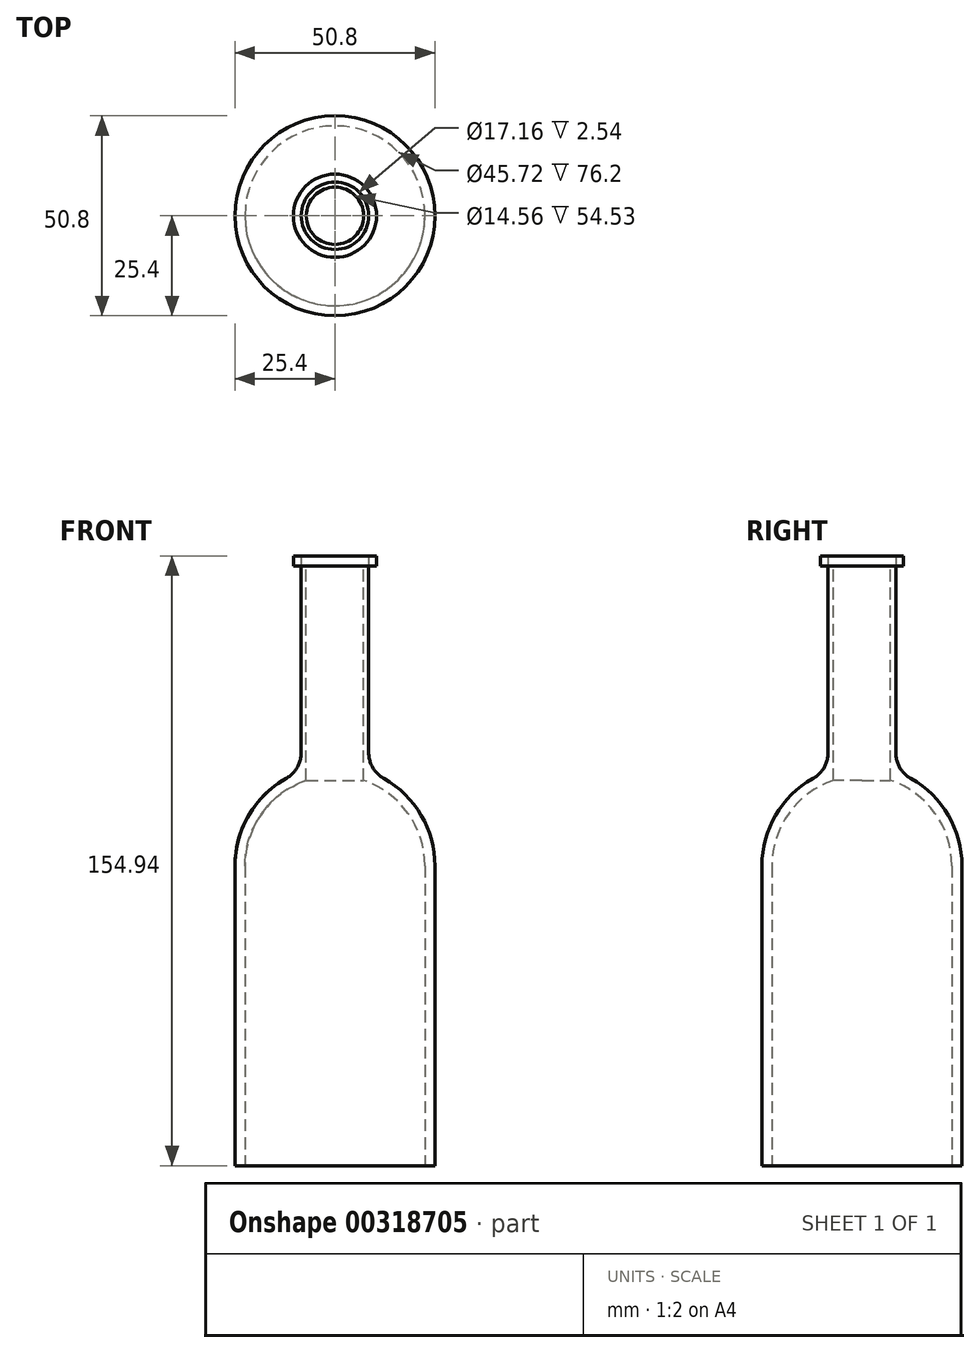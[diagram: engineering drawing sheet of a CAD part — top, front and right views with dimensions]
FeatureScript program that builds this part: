
annotation { "Feature Type Name" : "Feature", "Feature Type Description" : "" }
export const myFeature = defineFeature(function(context is Context, id is Id, definition is map)
    precondition{}
    {
        {
            var Q0;
            Q0=qCreatedBy(makeId("Top.planeOp"),FACE);
            var sketch = newSketch(context, id + "F0", { "sketchPlane" : qUnion([Q0])});
            skCircle(sketch, "E0", {"center": v(0, 0) * mm, "radius": 25.4 * mm});
            skSolve(sketch);
        }
        {
            var Q0;
            Q0=makeQuery(id+"F0.imprint","IMPRINT",FACE,{"disambiguationData":[TD([[makeQuery(id+"F0.imprint","IMPRINT",EDGE,{"derivedFrom":sQuery(id+"F0.wireOp",EDGE,"E0")}),1.0]])]});
            extrude(context, id + "F1", {"entities" : qUnion([Q0]), "depth" : 101.6 * mm});
        }
        {
            var Q0;
            Q0=makeQuery(id+"F1.opExtrude","CAP_EDGE",EDGE,{"disambiguationData":[OSD([sQuery(id+"F0.wireOp",EDGE,"E0")])],"isStart":false});
            fillet(context, id + "F2", {"entities" : qUnion([Q0]), "radius" : 25.4 * mm, "tangentPropagation" : true, "allowEdgeOverflow" : false});
        }
        {
            var Q0;
            Q0=qCreatedBy(makeId("Top.planeOp"),FACE);
            var sketch = newSketch(context, id + "F3", { "sketchPlane" : qUnion([Q0])});
            skCircle(sketch, "E1", {"center": v(0, 0) * mm, "radius": 8.58 * mm});
            skSolve(sketch);
        }
        {
            var Q0;
            Q0=makeQuery(id+"F3.imprint","IMPRINT",FACE,{"disambiguationData":[TD([[makeQuery(id+"F3.imprint","IMPRINT",EDGE,{"derivedFrom":sQuery(id+"F3.wireOp",EDGE,"E1")}),1.0]])]});
            extrude(context, id + "F4", {"entities" : qUnion([Q0]), "operationType" : NewBodyOperationType.ADD, "depth" : 152.4 * mm});
        }
        {
            var Q0;
            Q0=makeQuery(id+"F1.opExtrude","CAP_FACE",FACE,{"disambiguationData":[OSD([sQuery(id+"F0.wireOp",EDGE,"E0")])],"isStart":true});
            shell(context, id + "F5", {"entities" : qUnion([Q0]), "thickness" : 2.54 * mm});
        }
        {
            var Q0;
            Q0=makeQuery(id+"F4.boolean.opBoolean","INTERSECT",EDGE,{"derivedFrom":[makeQuery(id+"F2.opFillet","BLEND_FACE",FACE,{"disambiguationData":[OSD([sQuery(id+"F0.wireOp",EDGE,"E0")])]}),makeQuery(id+"F4.opExtrude","SWEPT_FACE",FACE,{"disambiguationData":[OSD([sQuery(id+"F3.wireOp",EDGE,"E1")])]})]});
            fillet(context, id + "F6", {"entities" : qUnion([Q0]), "radius" : 7.62 * mm, "tangentPropagation" : true, "allowEdgeOverflow" : false});
        }
        {
            var Q0;
            Q0=makeQuery(id+"F4.opExtrude","CAP_FACE",FACE,{"disambiguationData":[OSD([sQuery(id+"F3.wireOp",EDGE,"E1")])],"isStart":false});
            var sketch = newSketch(context, id + "F7", { "sketchPlane" : qUnion([Q0])});
            skCircle(sketch, "E2", {"center": v(0, 0) * mm, "radius": 10.57 * mm});
            skSolve(sketch);
        }
        {
            var Q0;
            Q0=makeQuery(id+"F7.imprint","IMPRINT",FACE,{"disambiguationData":[TD([[makeQuery(id+"F7.imprint","IMPRINT",EDGE,{"derivedFrom":sQuery(id+"F7.wireOp",EDGE,"E2")}),1.0]])]});
            extrude(context, id + "F8", {"entities" : qUnion([Q0]), "depth" : 2.54 * mm});
        }
        {
            var Q0;
            Q0=makeQuery(id+"F4.opExtrude","CAP_FACE",FACE,{"disambiguationData":[OSD([sQuery(id+"F3.wireOp",EDGE,"E1")])],"isStart":false});
            var sketch = newSketch(context, id + "F9", { "sketchPlane" : qUnion([Q0])});
            skCircle(sketch, "E3", {"center": v(0, 0) * mm, "radius": 7.28 * mm});
            skSolve(sketch);
        }
        {
            var Q0;
            Q0=makeQuery(id+"F9.imprint","IMPRINT",FACE,{"disambiguationData":[TD([[makeQuery(id+"F9.imprint","IMPRINT",EDGE,{"derivedFrom":sQuery(id+"F9.wireOp",EDGE,"E3")}),1.0]])]});
            extrude(context, id + "F10", {"entities" : qUnion([Q0]), "operationType" : NewBodyOperationType.REMOVE, "oppositeDirection" : true, "depth" : 76.2 * mm});
        }
    });
